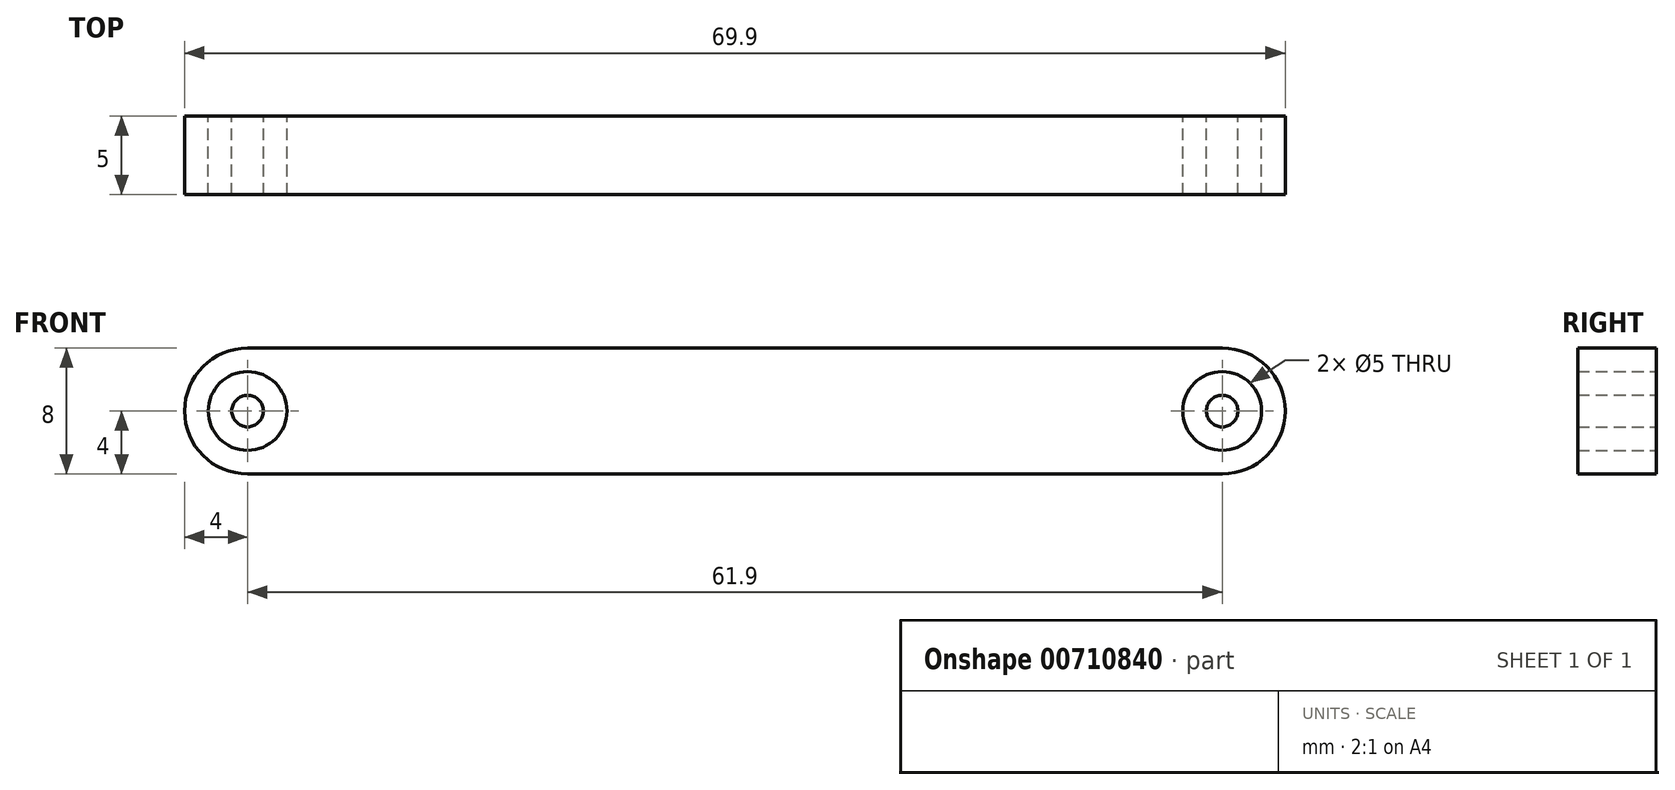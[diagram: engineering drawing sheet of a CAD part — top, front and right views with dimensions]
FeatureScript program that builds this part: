
annotation { "Feature Type Name" : "Feature", "Feature Type Description" : "" }
export const myFeature = defineFeature(function(context is Context, id is Id, definition is map)
    precondition{}
    {
        {
            var Q0;
            Q0=qCreatedBy(makeId("Front.planeOp"),FACE);
            var sketch = newSketch(context, id + "F0", { "sketchPlane" : qUnion([Q0])});
            skCircle(sketch, "E0", {"center": v(0, 0) * mm, "radius": 2.5 * mm});
            skCircle(sketch, "E1", {"center": v(0, 0) * mm, "radius": 1 * mm});
            skArc(sketch, "E2", {"start": v(0, 4) * mm, "mid": v(-4, 0) * mm, "end": v(0, -4) * mm});
            skCircle(sketch, "E3", {"center": v(61.9, 0) * mm, "radius": 1 * mm});
            skCircle(sketch, "E4", {"center": v(61.9, 0) * mm, "radius": 2.5 * mm});
            skArc(sketch, "E5", {"start": v(61.9, -4) * mm, "mid": v(65.9, 0) * mm, "end": v(61.9, 4) * mm});
            skLineSegment(sketch, "E6", {"start": v(0, 4) * mm, "end": v(61.9, 4) * mm});
            skLineSegment(sketch, "E7", {"start": v(0, -4) * mm, "end": v(61.9, -4) * mm});
            skSolve(sketch);
        }
        {
            var Q0;
            Q0=makeQuery(id+"F0.imprint","IMPRINT",FACE,{"disambiguationData":[TD([[makeQuery(id+"F0.imprint","IMPRINT",EDGE,{"derivedFrom":sQuery(id+"F0.wireOp",EDGE,"E0")}),-1.0]])]});
            var Q1;
            Q1=makeQuery(id+"F0.imprint","IMPRINT",FACE,{"disambiguationData":[TD([[makeQuery(id+"F0.imprint","IMPRINT",EDGE,{"derivedFrom":sQuery(id+"F0.wireOp",EDGE,"E1")}),1.0]])]});
            var Q2;
            Q2=makeQuery(id+"F0.imprint","IMPRINT",FACE,{"disambiguationData":[TD([[makeQuery(id+"F0.imprint","IMPRINT",EDGE,{"derivedFrom":sQuery(id+"F0.wireOp",EDGE,"E3")}),1.0]])]});
            extrude(context, id + "F1", {"entities" : qUnion([Q0, Q1, Q2]), "depth" : 5 * mm, "offsetDistance" : 25.4 * mm});
        }
    });
